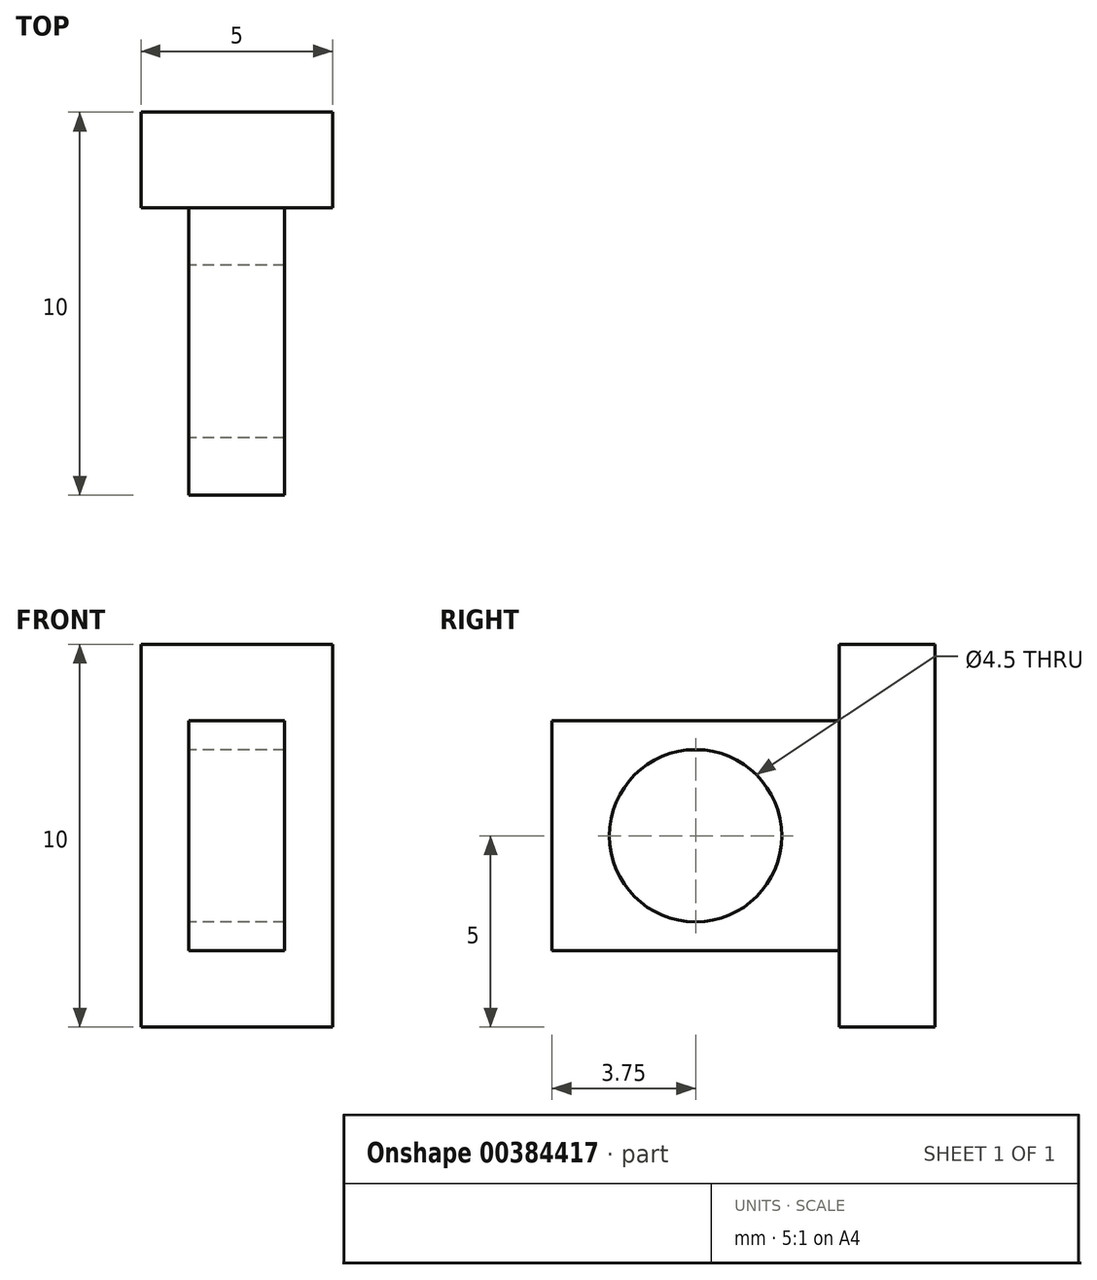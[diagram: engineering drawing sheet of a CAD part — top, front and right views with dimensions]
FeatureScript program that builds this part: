
annotation { "Feature Type Name" : "Feature", "Feature Type Description" : "" }
export const myFeature = defineFeature(function(context is Context, id is Id, definition is map)
    precondition{}
    {
        {
            var Q0;
            Q0=qCreatedBy(makeId("Front.planeOp"),FACE);
            var sketch = newSketch(context, id + "F0", { "sketchPlane" : qUnion([Q0])});
            skLineSegment(sketch, "E0.bottom", {"start": v(-2.5, 5) * mm, "end": v(2.5, 5) * mm});
            skLineSegment(sketch, "E0.top", {"start": v(-2.5, -5) * mm, "end": v(2.5, -5) * mm});
            skLineSegment(sketch, "E0.left", {"start": v(-2.5, 5) * mm, "end": v(-2.5, -5) * mm});
            skLineSegment(sketch, "E0.right", {"start": v(2.5, 5) * mm, "end": v(2.5, -5) * mm});
            skPoint(sketch, "E0.middle", {"position": v(0, 0) * mm});
            skSolve(sketch);
        }
        {
            var Q0;
            Q0=makeQuery(id+"F0.imprint","IMPRINT",FACE,{"disambiguationData":[TD([[makeQuery(id+"F0.imprint","IMPRINT",EDGE,{"derivedFrom":sQuery(id+"F0.wireOp",EDGE,"E0.bottom")}),-1.0]])]});
            extrude(context, id + "F1", {"entities" : qUnion([Q0]), "depth" : 2.5 * mm});
        }
        {
            var Q0;
            Q0=makeQuery(id+"F1.opExtrude","CAP_FACE",FACE,{"disambiguationData":[OSD([sQuery(id+"F0.wireOp",EDGE,"E0.bottom"),sQuery(id+"F0.wireOp",EDGE,"E0.top"),sQuery(id+"F0.wireOp",EDGE,"E0.left"),sQuery(id+"F0.wireOp",EDGE,"E0.right")])],"isStart":false});
            var sketch = newSketch(context, id + "F2", { "sketchPlane" : qUnion([Q0])});
            skLineSegment(sketch, "E1.bottom", {"start": v(1.25, 3) * mm, "end": v(-1.25, 3) * mm});
            skLineSegment(sketch, "E1.top", {"start": v(1.25, -3) * mm, "end": v(-1.25, -3) * mm});
            skLineSegment(sketch, "E1.left", {"start": v(1.25, 3) * mm, "end": v(1.25, -3) * mm});
            skLineSegment(sketch, "E1.right", {"start": v(-1.25, 3) * mm, "end": v(-1.25, -3) * mm});
            skPoint(sketch, "E1.middle", {"position": v(0, 0) * mm});
            skSolve(sketch);
        }
        {
            var Q0;
            Q0=makeQuery(id+"F2.imprint","IMPRINT",FACE,{"disambiguationData":[TD([[makeQuery(id+"F2.imprint","IMPRINT",EDGE,{"derivedFrom":sQuery(id+"F2.wireOp",EDGE,"E1.bottom")}),1.0]])]});
            extrude(context, id + "F3", {"entities" : qUnion([Q0]), "operationType" : NewBodyOperationType.ADD, "depth" : 7.5 * mm});
        }
        {
            var Q0;
            Q0=makeQuery(id+"F3.opExtrude","SWEPT_FACE",FACE,{"disambiguationData":[OSD([sQuery(id+"F2.wireOp",EDGE,"E1.right")])]});
            var sketch = newSketch(context, id + "F4", { "sketchPlane" : qUnion([Q0])});
            skCircle(sketch, "E2", {"center": v(6.25, 0) * mm, "radius": 2.25 * mm});
            skSolve(sketch);
        }
        {
            var Q0;
            Q0=makeQuery(id+"F4.imprint","IMPRINT",FACE,{"disambiguationData":[TD([[makeQuery(id+"F4.imprint","IMPRINT",EDGE,{"derivedFrom":sQuery(id+"F4.wireOp",EDGE,"E2")}),1.0]])]});
            extrude(context, id + "F5", {"entities" : qUnion([Q0]), "operationType" : NewBodyOperationType.REMOVE, "oppositeDirection" : true, "depth" : 3.44 * mm});
        }
    });
